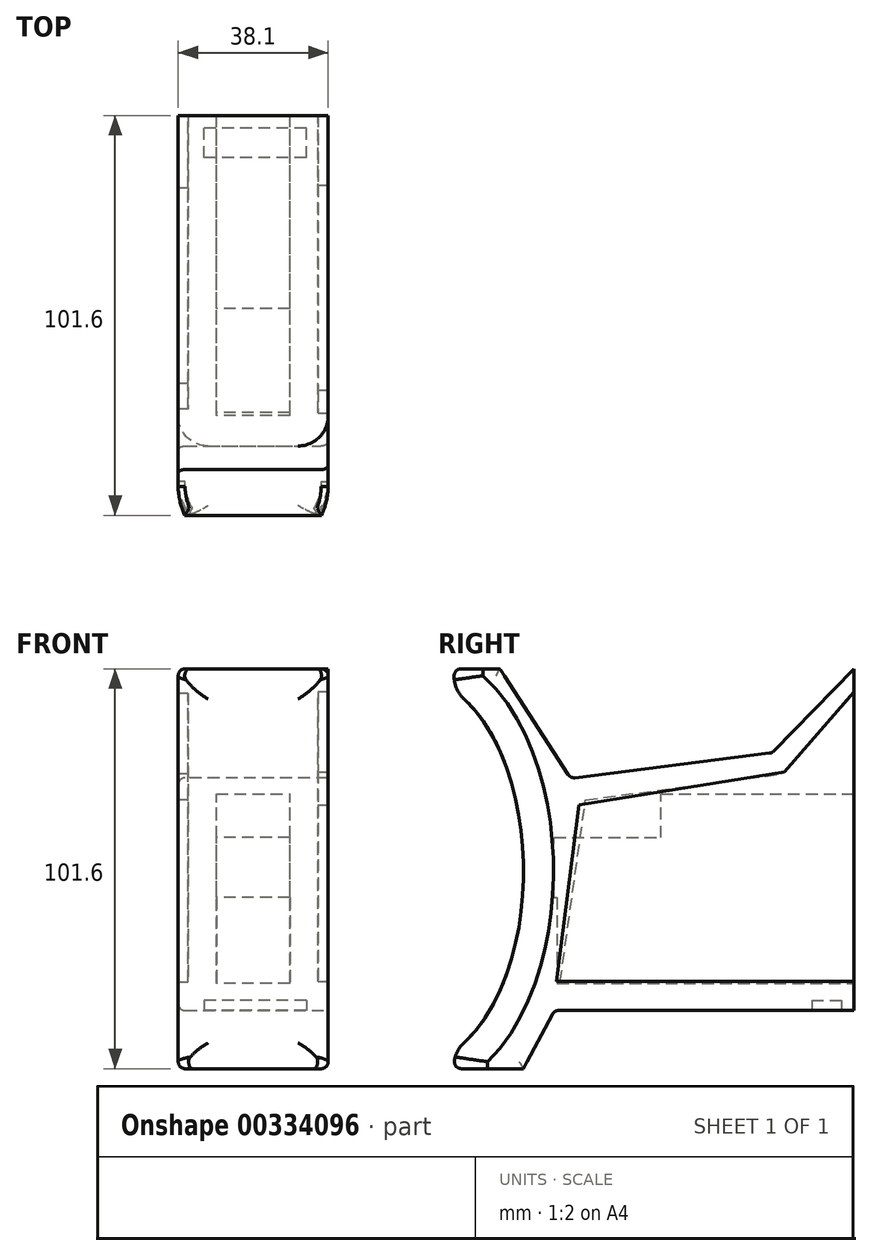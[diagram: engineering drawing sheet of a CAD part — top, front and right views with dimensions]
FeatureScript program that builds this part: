
annotation { "Feature Type Name" : "Feature", "Feature Type Description" : "" }
export const myFeature = defineFeature(function(context is Context, id is Id, definition is map)
    precondition{}
    {
        {
            var Q0;
            Q0=qCreatedBy(makeId("Top.planeOp"),FACE);
            var sketch = newSketch(context, id + "F0", { "sketchPlane" : qUnion([Q0])});
            skLineSegment(sketch, "E0.bottom", {"start": v(19.05, -50.8) * mm, "end": v(-19.05, -50.8) * mm});
            skLineSegment(sketch, "E0.top", {"start": v(19.05, 50.8) * mm, "end": v(-19.05, 50.8) * mm});
            skLineSegment(sketch, "E0.left", {"start": v(19.05, -50.8) * mm, "end": v(19.05, 50.8) * mm});
            skLineSegment(sketch, "E0.right", {"start": v(-19.05, -50.8) * mm, "end": v(-19.05, 50.8) * mm});
            skPoint(sketch, "E0.middle", {"position": v(0, 0) * mm});
            skSolve(sketch);
        }
        {
            var Q0;
            Q0=makeQuery(id+"F0.imprint","IMPRINT",FACE,{"disambiguationData":[TD([[makeQuery(id+"F0.imprint","IMPRINT",EDGE,{"derivedFrom":sQuery(id+"F0.wireOp",EDGE,"E0.bottom")}),-1.0]])]});
            extrude(context, id + "F1", {"entities" : qUnion([Q0]), "depth" : 101.6 * mm});
        }
        {
            var Q0;
            Q0=qCreatedBy(makeId("Right.planeOp"),FACE);
            var sketch = newSketch(context, id + "F2", { "sketchPlane" : qUnion([Q0])});
            skEllipse(sketch, "E1", {"center": v(-60.76, 50.25) * mm, "majorRadius": 48.96 * mm, "minorRadius": 27.58 * mm, "majorAxis": v(0, -1)});
            skSolve(sketch);
        }
        {
            var Q0;
            Q0=makeQuery(id+"F2.imprint","IMPRINT",FACE,{"disambiguationData":[TD([[makeQuery(id+"F2.imprint","IMPRINT",EDGE,{"derivedFrom":sQuery(id+"F2.wireOp",EDGE,"E1")}),1.0]])]});
            extrude(context, id + "F3", {"entities" : qUnion([Q0]), "operationType" : NewBodyOperationType.REMOVE, "depth" : 59.69 * mm});
        }
        {
            var Q0;
            Q0=makeQuery(id+"F2.imprint","IMPRINT",FACE,{"disambiguationData":[TD([[makeQuery(id+"F2.imprint","IMPRINT",EDGE,{"derivedFrom":sQuery(id+"F2.wireOp",EDGE,"E1")}),1.0]])]});
            extrude(context, id + "F4", {"entities" : qUnion([Q0]), "operationType" : NewBodyOperationType.REMOVE, "oppositeDirection" : true, "depth" : 25.4 * mm});
        }
        {
            var Q0;
            Q0=makeQuery(id+"F1.opExtrude","SWEPT_FACE",FACE,{"disambiguationData":[OSD([sQuery(id+"F0.wireOp",EDGE,"E0.left")])]});
            var sketch = newSketch(context, id + "F5", { "sketchPlane" : qUnion([Q0])});
            skLineSegment(sketch, "E2", {"start": v(50.8, 101.6) * mm, "end": v(29.96, 80.23) * mm});
            skLineSegment(sketch, "E3", {"start": v(-39.18, 101.6) * mm, "end": v(50.8, 101.6) * mm});
            skLineSegment(sketch, "E4", {"start": v(29.96, 80.23) * mm, "end": v(-21.2, 73.78) * mm});
            skLineSegment(sketch, "E5", {"start": v(-21.2, 73.78) * mm, "end": v(-39.18, 101.6) * mm});
            skSolve(sketch);
        }
        {
            var Q0;
            Q0=makeQuery(id+"F5.imprint","IMPRINT",FACE,{"disambiguationData":[TD([[makeQuery(id+"F5.imprint","IMPRINT",EDGE,{"derivedFrom":sQuery(id+"F5.wireOp",EDGE,"E2")}),-1.0]])]});
            extrude(context, id + "F6", {"entities" : qUnion([Q0]), "operationType" : NewBodyOperationType.REMOVE, "oppositeDirection" : true, "depth" : 73.15 * mm});
        }
        {
            var Q0;
            Q0=makeQuery(id+"F1.opExtrude","SWEPT_FACE",FACE,{"disambiguationData":[OSD([sQuery(id+"F0.wireOp",EDGE,"E0.left")])]});
            var sketch = newSketch(context, id + "F7", { "sketchPlane" : qUnion([Q0])});
            skLineSegment(sketch, "E6", {"start": v(-33.19, 0) * mm, "end": v(-25.35, 14.77) * mm});
            skLineSegment(sketch, "E7", {"start": v(-25.35, 14.77) * mm, "end": v(55.78, 14.77) * mm});
            skLineSegment(sketch, "E8", {"start": v(55.78, 14.77) * mm, "end": v(55.78, -6.9) * mm});
            skLineSegment(sketch, "E9", {"start": v(55.78, -6.9) * mm, "end": v(-33.19, 0) * mm});
            skSolve(sketch);
        }
        {
            var Q0;
            {var subQ0=sQuery(id+"F7.wireOp",EDGE,"E6");Q0=makeQuery(id+"F7.imprint","IMPRINT",FACE,{"disambiguationData":[TD([[makeQuery(id+"F7.imprint","IMPRINT",EDGE,{"derivedFrom":subQ0}),-1.0]])]});}
            extrude(context, id + "F8", {"entities" : qUnion([Q0]), "operationType" : NewBodyOperationType.REMOVE, "oppositeDirection" : true, "depth" : 107.95 * mm});
        }
        {
            var Q0;
            Q0=makeQuery(id+"F1.opExtrude","SWEPT_FACE",FACE,{"disambiguationData":[OSD([sQuery(id+"F0.wireOp",EDGE,"E0.left")])]});
            var sketch = newSketch(context, id + "F9", { "sketchPlane" : qUnion([Q0])});
            skLineSegment(sketch, "E10", {"start": v(-19.02, 67) * mm, "end": v(-24.78, 22.15) * mm});
            skLineSegment(sketch, "E11", {"start": v(-24.78, 22.15) * mm, "end": v(56.92, 22.15) * mm});
            skLineSegment(sketch, "E12", {"start": v(56.92, 22.15) * mm, "end": v(56.92, 102.7) * mm});
            skLineSegment(sketch, "E13", {"start": v(56.92, 102.7) * mm, "end": v(33.08, 75.4) * mm});
            skLineSegment(sketch, "E14", {"start": v(33.08, 75.4) * mm, "end": v(-19.02, 67) * mm});
            skSolve(sketch);
        }
        {
            var Q0;
            Q0 = qSketchRegion(id + "F9", true);
            extrude(context, id + "F10", {"entities" : qUnion([Q0]), "operationType" : NewBodyOperationType.REMOVE, "oppositeDirection" : true, "depth" : 2.54 * mm});
        }
        {
            var Q0;
            Q0=makeQuery(id+"F1.opExtrude","SWEPT_FACE",FACE,{"disambiguationData":[OSD([sQuery(id+"F0.wireOp",EDGE,"E0.right")])]});
            var sketch = newSketch(context, id + "F11", { "sketchPlane" : qUnion([Q0])});
            skLineSegment(sketch, "E15", {"start": v(-59.6, 105.13) * mm, "end": v(-59.6, 22.05) * mm});
            skLineSegment(sketch, "E16", {"start": v(-59.6, 22.05) * mm, "end": v(23.85, 22.05) * mm});
            skLineSegment(sketch, "E17", {"start": v(-32.36, 74.85) * mm, "end": v(-59.6, 105.13) * mm});
            skLineSegment(sketch, "E18", {"start": v(23.85, 22.05) * mm, "end": v(17.4, 68.29) * mm});
            skLineSegment(sketch, "E19", {"start": v(17.4, 68.29) * mm, "end": v(-32.36, 74.85) * mm});
            skSolve(sketch);
        }
        {
            var Q0;
            Q0 = qSketchRegion(id + "F11", true);
            extrude(context, id + "F12", {"entities" : qUnion([Q0]), "operationType" : NewBodyOperationType.REMOVE, "oppositeDirection" : true, "depth" : 2.54 * mm});
        }
        {
            var Q0;
            Q0=makeQuery(id+"F1.opExtrude","SWEPT_FACE",FACE,{"disambiguationData":[OSD([sQuery(id+"F0.wireOp",EDGE,"E0.top")])]});
            var sketch = newSketch(context, id + "F13", { "sketchPlane" : qUnion([Q0])});
            skLineSegment(sketch, "E20.bottom", {"start": v(9.34, 49.05) * mm, "end": v(-9.34, 49.05) * mm});
            skLineSegment(sketch, "E20.top", {"start": v(9.34, 69.83) * mm, "end": v(-9.34, 69.83) * mm});
            skLineSegment(sketch, "E20.left", {"start": v(9.34, 49.05) * mm, "end": v(9.34, 69.83) * mm});
            skLineSegment(sketch, "E20.right", {"start": v(-9.34, 49.05) * mm, "end": v(-9.34, 69.83) * mm});
            skPoint(sketch, "E20.middle", {"position": v(0, 59.44) * mm});
            skSolve(sketch);
        }
        {
            var Q0;
            Q0 = qSketchRegion(id + "F13", true);
            extrude(context, id + "F14", {"entities" : qUnion([Q0]), "operationType" : NewBodyOperationType.REMOVE, "oppositeDirection" : true, "depth" : 49.02 * mm});
        }
        {
            var Q0;
            Q0=makeQuery(id+"F1.opExtrude","SWEPT_FACE",FACE,{"disambiguationData":[OSD([sQuery(id+"F0.wireOp",EDGE,"E0.top")])]});
            var sketch = newSketch(context, id + "F15", { "sketchPlane" : qUnion([Q0])});
            skLineSegment(sketch, "E21.bottom", {"start": v(-9.34, 49.05) * mm, "end": v(9.34, 49.05) * mm});
            skLineSegment(sketch, "E21.top", {"start": v(-9.34, 21.69) * mm, "end": v(9.34, 21.69) * mm});
            skLineSegment(sketch, "E21.left", {"start": v(-9.34, 49.05) * mm, "end": v(-9.34, 21.69) * mm});
            skLineSegment(sketch, "E21.right", {"start": v(9.34, 49.05) * mm, "end": v(9.34, 21.69) * mm});
            skSolve(sketch);
        }
        {
            var Q0;
            Q0 = qSketchRegion(id + "F15", true);
            extrude(context, id + "F16", {"entities" : qUnion([Q0]), "operationType" : NewBodyOperationType.REMOVE, "oppositeDirection" : true, "depth" : 75.44 * mm});
        }
        {
            var Q0;
            Q0=makeQuery(id+"F1.opExtrude","SWEPT_FACE",FACE,{"disambiguationData":[OSD([sQuery(id+"F0.wireOp",EDGE,"E0.top")])]});
            var sketch = newSketch(context, id + "F17", { "sketchPlane" : qUnion([Q0])});
            skPoint(sketch, "E22.firstSnap0", {"position": v(16.51, 58.7) * mm});
            skLineSegment(sketch, "E22.bottom", {"start": v(-9.34, 58.7) * mm, "end": v(9.34, 58.7) * mm});
            skLineSegment(sketch, "E22.top", {"start": v(-9.34, 43.48) * mm, "end": v(9.34, 43.48) * mm});
            skLineSegment(sketch, "E22.left", {"start": v(-9.34, 58.7) * mm, "end": v(-9.34, 43.48) * mm});
            skLineSegment(sketch, "E22.right", {"start": v(9.34, 58.7) * mm, "end": v(9.34, 43.48) * mm});
            skSolve(sketch);
        }
        {
            var Q0;
            Q0 = qSketchRegion(id + "F17", true);
            extrude(context, id + "F18", {"entities" : qUnion([Q0]), "operationType" : NewBodyOperationType.REMOVE, "oppositeDirection" : true, "depth" : 76.2 * mm});
        }
        {
            var Q0;
            Q0=makeQuery(id+"F6.boolean.opBoolean","COPY",EDGE,{"derivedFrom":makeQuery(id+"F6.opExtrude","CAP_EDGE",EDGE,{"disambiguationData":[OSD([sQuery(id+"F5.wireOp",EDGE,"E4")])],"isStart":true})});
            var Q1;
            Q1=makeQuery(id+"F6.boolean.opBoolean","INTERSECT",EDGE,{"derivedFrom":[makeQuery(id+"F1.opExtrude","SWEPT_FACE",FACE,{"disambiguationData":[OSD([sQuery(id+"F0.wireOp",EDGE,"E0.right")])]}),makeQuery(id+"F6.opExtrude","SWEPT_FACE",FACE,{"disambiguationData":[OSD([sQuery(id+"F5.wireOp",EDGE,"E4")])]})]});
            var Q2;
            Q2=makeQuery(id+"F6.boolean.opBoolean","INTERSECT",EDGE,{"derivedFrom":[makeQuery(id+"F1.opExtrude","SWEPT_FACE",FACE,{"disambiguationData":[OSD([sQuery(id+"F0.wireOp",EDGE,"E0.right")])]}),makeQuery(id+"F6.opExtrude","SWEPT_FACE",FACE,{"disambiguationData":[OSD([sQuery(id+"F5.wireOp",EDGE,"E5")])]})]});
            var Q3;
            Q3=makeQuery(id+"F1.opExtrude","CAP_EDGE",EDGE,{"disambiguationData":[OSD([sQuery(id+"F0.wireOp",EDGE,"E0.right")])],"isStart":false});
            var Q4;
            Q4=makeQuery(id+"F1.opExtrude","CAP_EDGE",EDGE,{"disambiguationData":[OSD([sQuery(id+"F0.wireOp",EDGE,"E0.left")])],"isStart":false});
            var Q5;
            Q5=makeQuery(id+"F6.boolean.opBoolean","COPY",EDGE,{"derivedFrom":makeQuery(id+"F6.opExtrude","SWEPT_EDGE",EDGE,{"disambiguationData":[OSD([sQuery(id+"F0.wireOp",EDGE,"E0.left"),sQuery(id+"F5.wireOp",EDGE,"E3"),sQuery(id+"F5.wireOp",EDGE,"E5")])]})});
            var Q6;
            Q6=makeQuery(id+"F1.opExtrude","CAP_EDGE",EDGE,{"disambiguationData":[OSD([sQuery(id+"F0.wireOp",EDGE,"E0.bottom")])],"isStart":false});
            var Q7;
            Q7=makeQuery(id+"F6.boolean.opBoolean","COPY",EDGE,{"derivedFrom":makeQuery(id+"F6.opExtrude","CAP_EDGE",EDGE,{"disambiguationData":[OSD([sQuery(id+"F5.wireOp",EDGE,"E5")])],"isStart":true})});
            var Q8;
            Q8=makeQuery(id+"F6.boolean.opBoolean","COPY",EDGE,{"derivedFrom":makeQuery(id+"F6.opExtrude","CAP_EDGE",EDGE,{"disambiguationData":[OSD([sQuery(id+"F5.wireOp",EDGE,"E2")])],"isStart":true})});
            var Q9;
            Q9=makeQuery(id+"F6.boolean.opBoolean","COPY",EDGE,{"derivedFrom":makeQuery(id+"F6.opExtrude","SWEPT_EDGE",EDGE,{"disambiguationData":[OSD([sQuery(id+"F5.wireOp",EDGE,"E4"),sQuery(id+"F5.wireOp",EDGE,"E5")])]})});
            var Q10;
            Q10=makeQuery(id+"F6.boolean.opBoolean","COPY",EDGE,{"derivedFrom":makeQuery(id+"F6.opExtrude","SWEPT_EDGE",EDGE,{"disambiguationData":[OSD([sQuery(id+"F5.wireOp",EDGE,"E2"),sQuery(id+"F5.wireOp",EDGE,"E4")])]})});
            var Q11;
            Q11=makeQuery(id+"F6.boolean.opBoolean","INTERSECT",EDGE,{"derivedFrom":[makeQuery(id+"F1.opExtrude","SWEPT_FACE",FACE,{"disambiguationData":[OSD([sQuery(id+"F0.wireOp",EDGE,"E0.right")])]}),makeQuery(id+"F6.opExtrude","SWEPT_FACE",FACE,{"disambiguationData":[OSD([sQuery(id+"F5.wireOp",EDGE,"E2")])]})]});
            fillet(context, id + "F19", {"entities" : qUnion([Q0, Q1, Q2, Q3, Q4, Q5, Q6, Q7, Q8, Q9, Q10, Q11]), "radius" : 1.78 * mm, "tangentPropagation" : true, "allowEdgeOverflow" : false});
        }
        {
            var Q0;
            Q0=makeQuery(id+"F3.boolean.opBoolean","INTERSECT",EDGE,{"derivedFrom":[makeQuery(id+"F1.opExtrude","SWEPT_FACE",FACE,{"disambiguationData":[OSD([sQuery(id+"F0.wireOp",EDGE,"E0.left")])]}),makeQuery(id+"F3.opExtrude","SWEPT_FACE",FACE,{"disambiguationData":[OSD([sQuery(id+"F2.wireOp",EDGE,"E1")])]})]});
            var Q1;
            Q1=makeQuery(id+"F4.boolean.opBoolean","INTERSECT",EDGE,{"disambiguationData":[OD(1.0)],"derivedFrom":[makeQuery(id+"F1.opExtrude","SWEPT_FACE",FACE,{"disambiguationData":[OSD([sQuery(id+"F0.wireOp",EDGE,"E0.bottom")])]}),makeQuery(id+"F4.opExtrude","SWEPT_FACE",FACE,{"disambiguationData":[OSD([sQuery(id+"F2.wireOp",EDGE,"E1")])]})]});
            var Q2;
            Q2=makeQuery(id+"F4.boolean.opBoolean","INTERSECT",EDGE,{"derivedFrom":[makeQuery(id+"F1.opExtrude","SWEPT_FACE",FACE,{"disambiguationData":[OSD([sQuery(id+"F0.wireOp",EDGE,"E0.right")])]}),makeQuery(id+"F4.opExtrude","SWEPT_FACE",FACE,{"disambiguationData":[OSD([sQuery(id+"F2.wireOp",EDGE,"E1")])]})]});
            var Q3;
            Q3=makeQuery(id+"F4.boolean.opBoolean","INTERSECT",EDGE,{"disambiguationData":[OD(0.0)],"derivedFrom":[makeQuery(id+"F1.opExtrude","SWEPT_FACE",FACE,{"disambiguationData":[OSD([sQuery(id+"F0.wireOp",EDGE,"E0.bottom")])]}),makeQuery(id+"F4.opExtrude","SWEPT_FACE",FACE,{"disambiguationData":[OSD([sQuery(id+"F2.wireOp",EDGE,"E1")])]})]});
            fillet(context, id + "F20", {"entities" : qUnion([Q0, Q1, Q2, Q3]), "radius" : 7.62 * mm, "tangentPropagation" : true, "allowEdgeOverflow" : false});
        }
        {
            var Q0;
            Q0=makeQuery(id+"F8.boolean.opBoolean","COPY",EDGE,{"derivedFrom":makeQuery(id+"F8.opExtrude","CAP_EDGE",EDGE,{"disambiguationData":[OSD([sQuery(id+"F7.wireOp",EDGE,"E7")])],"isStart":true})});
            var Q1;
            Q1=makeQuery(id+"F1.opExtrude","CAP_EDGE",EDGE,{"disambiguationData":[OSD([sQuery(id+"F0.wireOp",EDGE,"E0.left")])],"isStart":true});
            var Q2;
            {var subQ0=sQuery(id+"F0.wireOp",EDGE,"E0.left");Q2=makeQuery(id+"F20.opFillet","BLEND_EDGE",EDGE,{"blendedFrom":[makeQuery(id+"F3.boolean.opBoolean","INTERSECT",EDGE,{"derivedFrom":[makeQuery(id+"F1.opExtrude","SWEPT_FACE",FACE,{"disambiguationData":[OSD([subQ0])]}),makeQuery(id+"F3.opExtrude","SWEPT_FACE",FACE,{"disambiguationData":[OSD([sQuery(id+"F2.wireOp",EDGE,"E1")])]})]}),makeQuery(id+"F19.opFillet","BLEND_FACE",FACE,{"disambiguationData":[OSD([subQ0])]})],"blendedInto":[makeQuery(id+"F19.opFillet","BLEND_FACE",FACE,{"disambiguationData":[OSD([subQ0])]})]});}
            var Q3;
            {var subQ0=sQuery(id+"F0.wireOp",EDGE,"E0.right");Q3=makeQuery(id+"F20.opFillet","BLEND_EDGE",EDGE,{"blendedFrom":[makeQuery(id+"F4.boolean.opBoolean","INTERSECT",EDGE,{"derivedFrom":[makeQuery(id+"F1.opExtrude","SWEPT_FACE",FACE,{"disambiguationData":[OSD([subQ0])]}),makeQuery(id+"F4.opExtrude","SWEPT_FACE",FACE,{"disambiguationData":[OSD([sQuery(id+"F2.wireOp",EDGE,"E1")])]})]}),makeQuery(id+"F19.opFillet","BLEND_FACE",FACE,{"disambiguationData":[OSD([subQ0])]})],"blendedInto":[makeQuery(id+"F19.opFillet","BLEND_FACE",FACE,{"disambiguationData":[OSD([subQ0])]})]});}
            var Q4;
            {var subQ0=sQuery(id+"F0.wireOp",EDGE,"E0.right");Q4=makeQuery(id+"F20.opFillet","BLEND_EDGE",EDGE,{"blendedFrom":[makeQuery(id+"F4.boolean.opBoolean","INTERSECT",EDGE,{"derivedFrom":[makeQuery(id+"F1.opExtrude","SWEPT_FACE",FACE,{"disambiguationData":[OSD([subQ0])]}),makeQuery(id+"F4.opExtrude","SWEPT_FACE",FACE,{"disambiguationData":[OSD([sQuery(id+"F2.wireOp",EDGE,"E1")])]})]}),makeQuery(id+"F1.opExtrude","CAP_FACE",FACE,{"disambiguationData":[OSD([sQuery(id+"F0.wireOp",EDGE,"E0.bottom"),sQuery(id+"F0.wireOp",EDGE,"E0.top"),sQuery(id+"F0.wireOp",EDGE,"E0.left"),subQ0])],"isStart":true})],"blendedInto":[makeQuery(id+"F1.opExtrude","CAP_FACE",FACE,{"disambiguationData":[OSD([sQuery(id+"F0.wireOp",EDGE,"E0.bottom"),sQuery(id+"F0.wireOp",EDGE,"E0.top"),sQuery(id+"F0.wireOp",EDGE,"E0.left"),subQ0])],"isStart":true})]});}
            var Q5;
            Q5=makeQuery(id+"F1.opExtrude","CAP_EDGE",EDGE,{"disambiguationData":[OSD([sQuery(id+"F0.wireOp",EDGE,"E0.bottom")])],"isStart":true});
            var Q6;
            Q6=makeQuery(id+"F8.boolean.opBoolean","COPY",EDGE,{"derivedFrom":makeQuery(id+"F8.opExtrude","SWEPT_EDGE",EDGE,{"disambiguationData":[OSD([sQuery(id+"F0.wireOp",EDGE,"E0.left"),sQuery(id+"F7.wireOp",EDGE,"E6"),sQuery(id+"F7.wireOp",EDGE,"E9")])]})});
            var Q7;
            Q7=makeQuery(id+"F8.boolean.opBoolean","COPY",EDGE,{"derivedFrom":makeQuery(id+"F8.opExtrude","SWEPT_EDGE",EDGE,{"disambiguationData":[OSD([sQuery(id+"F7.wireOp",EDGE,"E6"),sQuery(id+"F7.wireOp",EDGE,"E7")])]})});
            var Q8;
            Q8=makeQuery(id+"F8.boolean.opBoolean","COPY",EDGE,{"derivedFrom":makeQuery(id+"F8.opExtrude","CAP_EDGE",EDGE,{"disambiguationData":[OSD([sQuery(id+"F7.wireOp",EDGE,"E6")])],"isStart":true})});
            var Q9;
            Q9=makeQuery(id+"F8.boolean.opBoolean","INTERSECT",EDGE,{"derivedFrom":[makeQuery(id+"F1.opExtrude","SWEPT_FACE",FACE,{"disambiguationData":[OSD([sQuery(id+"F0.wireOp",EDGE,"E0.right")])]}),makeQuery(id+"F8.opExtrude","SWEPT_FACE",FACE,{"disambiguationData":[OSD([sQuery(id+"F7.wireOp",EDGE,"E6")])]})]});
            var Q10;
            Q10=makeQuery(id+"F8.boolean.opBoolean","INTERSECT",EDGE,{"derivedFrom":[makeQuery(id+"F1.opExtrude","SWEPT_FACE",FACE,{"disambiguationData":[OSD([sQuery(id+"F0.wireOp",EDGE,"E0.right")])]}),makeQuery(id+"F8.opExtrude","SWEPT_FACE",FACE,{"disambiguationData":[OSD([sQuery(id+"F7.wireOp",EDGE,"E7")])]})]});
            fillet(context, id + "F21", {"entities" : qUnion([Q0, Q1, Q2, Q3, Q4, Q5, Q6, Q7, Q8, Q9, Q10]), "radius" : 1.78 * mm, "tangentPropagation" : true, "allowEdgeOverflow" : false});
        }
        {
            var Q0;
            Q0=makeQuery(id+"F8.boolean.opBoolean","COPY",FACE,{"derivedFrom":makeQuery(id+"F8.opExtrude","SWEPT_FACE",FACE,{"disambiguationData":[OSD([sQuery(id+"F7.wireOp",EDGE,"E7")])]})});
            var sketch = newSketch(context, id + "F22", { "sketchPlane" : qUnion([Q0])});
            skLineSegment(sketch, "E23.bottom", {"start": v(13.51, -40.05) * mm, "end": v(-12.52, -40.05) * mm});
            skLineSegment(sketch, "E23.top", {"start": v(13.51, -47.61) * mm, "end": v(-12.52, -47.61) * mm});
            skLineSegment(sketch, "E23.left", {"start": v(13.51, -40.05) * mm, "end": v(13.51, -47.61) * mm});
            skLineSegment(sketch, "E23.right", {"start": v(-12.52, -40.05) * mm, "end": v(-12.52, -47.61) * mm});
            skSolve(sketch);
        }
        {
            var Q0;
            Q0 = qSketchRegion(id + "F22", true);
            extrude(context, id + "F23", {"entities" : qUnion([Q0]), "operationType" : NewBodyOperationType.REMOVE, "oppositeDirection" : true, "depth" : 2.54 * mm});
        }
    });
